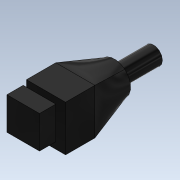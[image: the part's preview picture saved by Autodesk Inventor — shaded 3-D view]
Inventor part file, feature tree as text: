
AUTODESK INVENTOR PART (.ipt)
format: ipt  version: 2020.2 (Build 242310000, 310)  size: 143,872 bytes
history: native  units: in
note: dims shown in document units (in); Inventor stores cm internally (conversion verified against a paired STEP export)
features: sketch x5, extrude x3, plane x1, loft x1, projected_geometry x1
ambient origin geometry x8: Origin, YZ Plane, XZ Plane, XY Plane, X Axis, Y Axis, Z Axis, Center Point
bodies: Solid1 (feature_tree)
feature tree (11):
  extrude  "Extrusion1"  Depth=0.4724in TaperAngle=0.0deg
  sketch  "Sketch2"  dims[d3=0.3937in d4=0.4724in]
  plane  "Work Plane1"
  loft  "Loft1"
  extrude  "Extrusion2"  Depth=0.4724in
  extrude  "Extrusion3"  TaperAngle=0.0deg  [1 undecoded]
  sketch  "Sketch1"  dims[d0=0.2165in d1=0.4724in d2=0.0in]
  sketch  "Sketch3"  dims[d5=0.4724in d6=0.5512in]
  sketch  "Sketch4"  dims[d7=0.0in d8=90.0deg d9=0.0in d10=90.0deg]
  projected_geometry  "Projected Loop1"
  sketch  "Sketch5"  dims[d11=0.3543in d12=0.0in d13=0.3937in d14=0.3937in d15=0.0394in d16=0.1969in d17=0.0in]
note: 1 required parameter value undecoded (feature->parameter linkage not recoverable at this tier; creation-order binding heuristic only, values carry confidence <= 0.55)
